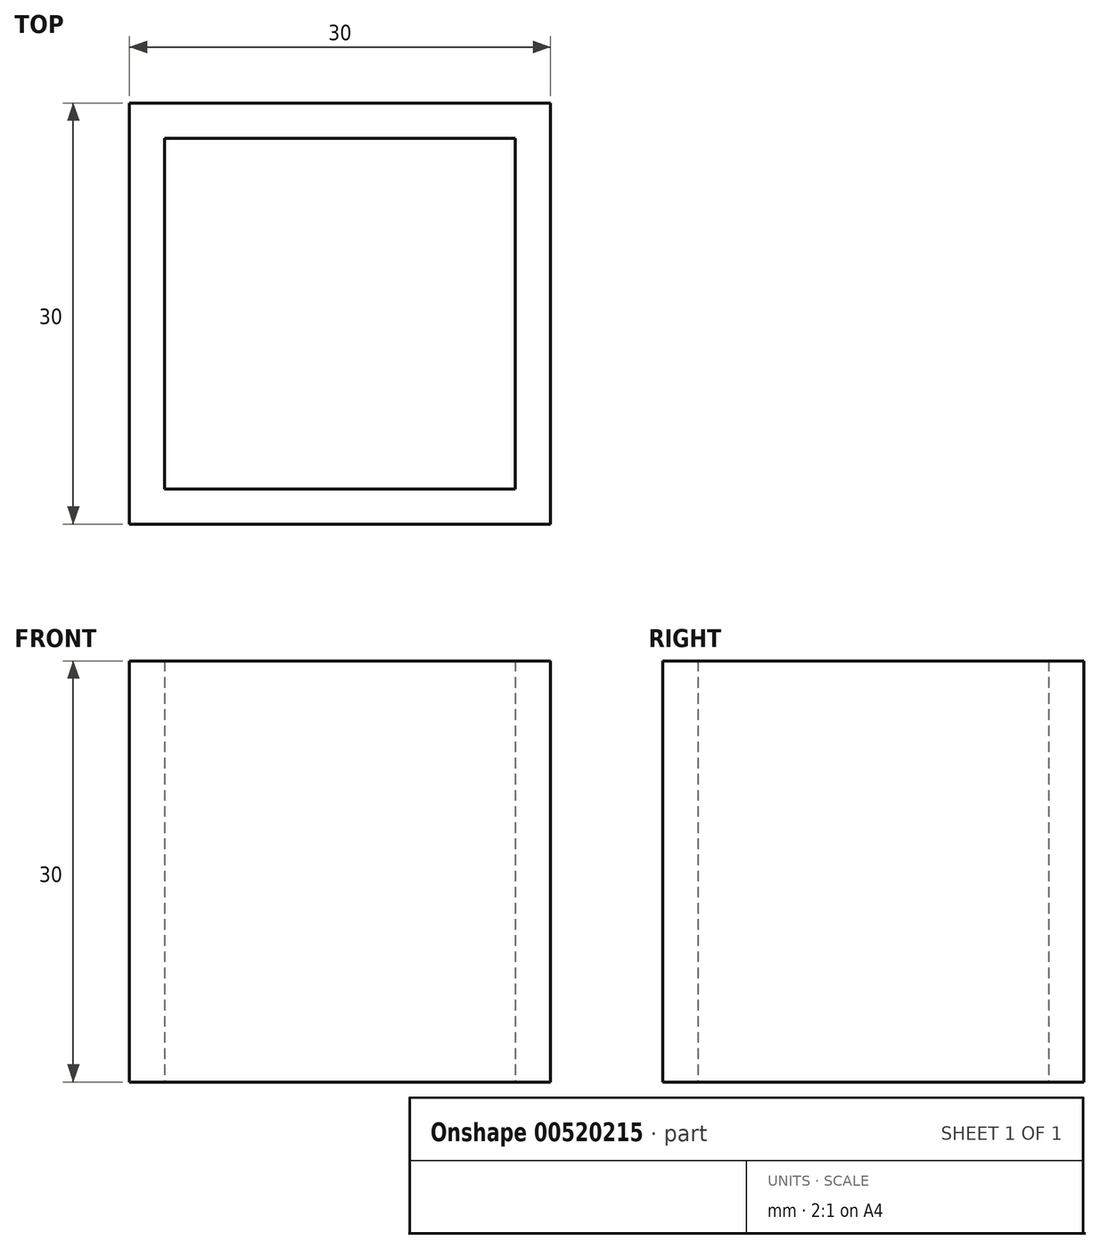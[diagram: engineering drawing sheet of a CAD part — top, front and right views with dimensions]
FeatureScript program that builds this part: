
annotation { "Feature Type Name" : "Feature", "Feature Type Description" : "" }
export const myFeature = defineFeature(function(context is Context, id is Id, definition is map)
    precondition{}
    {
        {
            var Q0;
            Q0=qCreatedBy(makeId("Top.planeOp"),FACE);
            var sketch = newSketch(context, id + "F0", { "sketchPlane" : qUnion([Q0])});
            skLineSegment(sketch, "E0.bottom", {"start": v(-30, 0) * mm, "end": v(0, 0) * mm});
            skLineSegment(sketch, "E0.top", {"start": v(-30, -30) * mm, "end": v(0, -30) * mm});
            skLineSegment(sketch, "E0.left", {"start": v(-30, 0) * mm, "end": v(-30, -30) * mm});
            skLineSegment(sketch, "E0.right", {"start": v(0, 0) * mm, "end": v(0, -30) * mm});
            skLineSegment(sketch, "E1.0", {"start": v(-27.5, -2.5) * mm, "end": v(-2.5, -2.5) * mm});
            skLineSegment(sketch, "E1.1", {"start": v(-27.5, -2.5) * mm, "end": v(-27.5, -27.5) * mm});
            skLineSegment(sketch, "E1.2", {"start": v(-27.5, -27.5) * mm, "end": v(-2.5, -27.5) * mm});
            skLineSegment(sketch, "E1.3", {"start": v(-2.5, -2.5) * mm, "end": v(-2.5, -27.5) * mm});
            skSolve(sketch);
        }
        {
            var Q0;
            Q0=makeQuery(id+"F0.imprint","IMPRINT",FACE,{"disambiguationData":[TD([[makeQuery(id+"F0.imprint","IMPRINT",EDGE,{"derivedFrom":sQuery(id+"F0.wireOp",EDGE,"E0.bottom")}),-1.0]])]});
            extrude(context, id + "F1", {"entities" : qUnion([Q0]), "depth" : 30 * mm, "offsetDistance" : 25 * mm});
        }
    });
